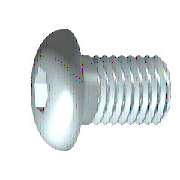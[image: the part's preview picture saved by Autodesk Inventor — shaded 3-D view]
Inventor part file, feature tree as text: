
AUTODESK INVENTOR PART (.ipt)
format: ipt  version: 2021 (Build 250183000, 183)  size: 203,776 bytes
history: native  units: mm (DEFAULTED — no unit token found)
features: sketch x2, extrude x1, plane x1, fillet x1
ambient origin geometry x7: Origin, YZ Plane, XY Plane, X Axis, Y Axis, Z Axis, Center Point
bodies: Solid1 (feature_tree), Body (feature_tree)
feature tree (5):
  extrude  "Slot"  Depth=1.65mm
  plane  "Work Plane1"
  fillet  "Fillet2"  Radius=1.65mm
  sketch  "Sketch1"  dims[d1=6.5mm d2=0.306825mm d3=1.65mm]
  sketch  "Sketch2"  dims[d4=1.04mm d5=60.0deg d6=3.0mm d7=3.0mm d8=2.309401mm d9=5.7mm d10=90.0deg d11=10.0mm d12=0.0mm d13=6.5mm d14=0.0mm d15=0.306725mm d16=0.306725mm d17=1.45mm d19=0.0mm d26=8.0mm d27=45.0deg d28=0.0mm d29=0.0mm d30=0.3mm]
